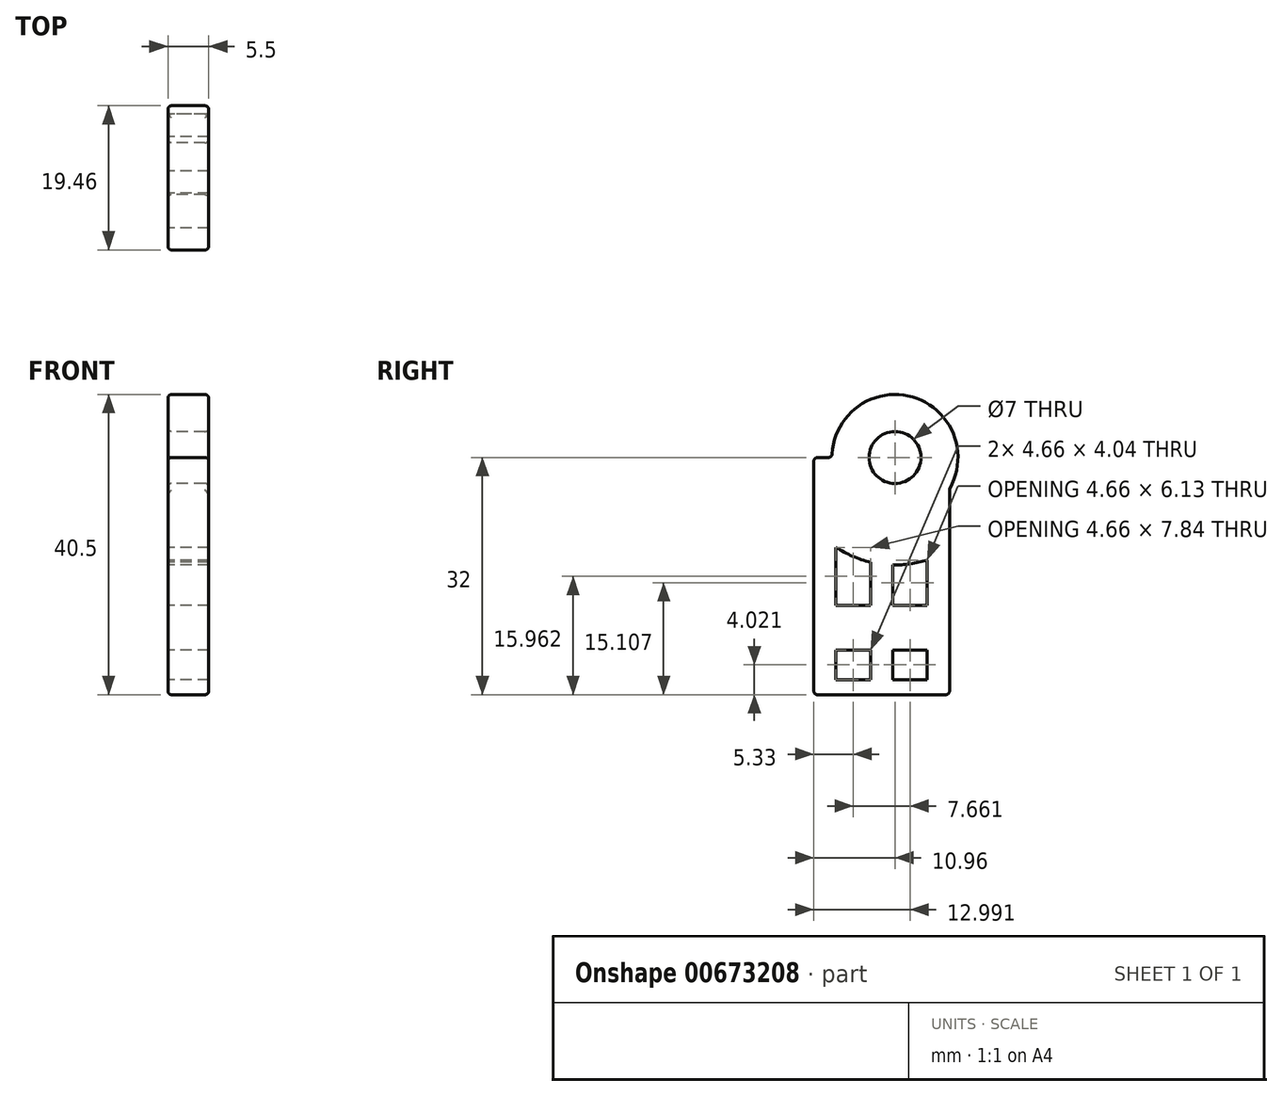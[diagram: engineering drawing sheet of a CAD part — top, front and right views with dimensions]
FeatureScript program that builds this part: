
annotation { "Feature Type Name" : "Feature", "Feature Type Description" : "" }
export const myFeature = defineFeature(function(context is Context, id is Id, definition is map)
    precondition{}
    {
        {
            var Q0;
            Q0=qCreatedBy(makeId("Right.planeOp"),FACE);
            var sketch = newSketch(context, id + "F0", { "sketchPlane" : qUnion([Q0])});
            skCircle(sketch, "E0", {"center": v(0, 0) * mm, "radius": 8.5 * mm});
            skLineSegment(sketch, "E1.bottom", {"start": v(-10.96, 0) * mm, "end": v(-8.5, 0) * mm});
            skLineSegment(sketch, "E1.left", {"start": v(-10.96, 0) * mm, "end": v(-10.96, -30) * mm});
            skLineSegment(sketch, "E2", {"start": v(-0.43, -4.25) * mm, "end": v(7.36, -4.25) * mm, "construction": true});
            skLineSegment(sketch, "E3", {"start": v(7.36, -4.25) * mm, "end": v(7.36, -30) * mm});
            skLineSegment(sketch, "E4", {"start": v(7.36, -30) * mm, "end": v(-10.96, -30) * mm});
            skCircle(sketch, "E5", {"center": v(0, 0) * mm, "radius": 3.5 * mm});
            skSolve(sketch);
        }
        {
            var Q0;
            Q0=makeQuery(id+"F0.imprint","IMPRINT",FACE,{"disambiguationData":[TD([[makeQuery(id+"F0.imprint","IMPRINT",EDGE,{"derivedFrom":sQuery(id+"F0.wireOp",EDGE,"E5")}),-1.0]])]});
            var Q1;
            {var subQ1=sQuery(id+"F0.wireOp",EDGE,"E1.bottom");Q1=makeQuery(id+"F0.imprint","IMPRINT",FACE,{"disambiguationData":[TD([[makeQuery(id+"F0.imprint","IMPRINT",EDGE,{"derivedFrom":subQ1}),-1.0]])]});}
            extrude(context, id + "F1", {"entities" : qUnion([Q0, Q1]), "depth" : 5.5 * mm});
        }
        {
            var Q0;
            {var subQ0=sQuery(id+"F0.wireOp",EDGE,"E4");var subQ1=sQuery(id+"F0.wireOp",EDGE,"E1.left");Q0=makeQuery(id+"FtR0d7urNmnyYv5_1.boolean.opBoolean","MERGE",FACE,{"derivedFrom":[makeQuery(id+"F9VDkFG8JvXqduY_1.boolean.opBoolean","MERGE",FACE,{"derivedFrom":[makeQuery(id+"F1.opExtrude","SWEPT_FACE",FACE,{"disambiguationData":[OSD([subQ0])]}),makeQuery(id+"F9VDkFG8JvXqduY_1.opExtrude","SWEPT_FACE",FACE,{"disambiguationData":[OSD([subQ1,subQ0])]})]}),makeQuery(id+"FtR0d7urNmnyYv5_1.opExtrude","SWEPT_FACE",FACE,{"disambiguationData":[OSD([subQ1,subQ0])]})]});}
            extrude(context, id + "F2", {"entities" : qUnion([Q0]), "operationType" : NewBodyOperationType.ADD, "depth" : 3 * mm});
        }
        {
            var Q0;
            {var subQ0=sQuery(id+"F0.wireOp",EDGE,"E4");Q0=makeQuery(id+"F2.boolean.opBoolean","MERGE",FACE,{"derivedFrom":[makeQuery(id+"F1.opExtrude","CAP_FACE",FACE,{"disambiguationData":[OSD([sQuery(id+"F0.wireOp",EDGE,"E0"),sQuery(id+"F0.wireOp",EDGE,"E1.bottom"),sQuery(id+"F0.wireOp",EDGE,"E1.left"),sQuery(id+"F0.wireOp",EDGE,"E3"),subQ0,sQuery(id+"F0.wireOp",EDGE,"E5")])],"isStart":true}),makeQuery(id+"F2.opExtrude","SWEPT_FACE",FACE,{"disambiguationData":[OSD([subQ0]),TDD([makeQuery(id+"F1.opExtrude","CAP_EDGE",EDGE,{"disambiguationData":[OSD([subQ0])],"isStart":true})])]})]});}
            var sketch = newSketch(context, id + "F3", { "sketchPlane" : qUnion([Q0])});
            skArc(sketch, "E6", {"start": v(-7.36, -8.84) * mm, "mid": v(3.22, -11.04) * mm, "end": v(10.96, -3.48) * mm});
            skLineSegment(sketch, "E7", {"start": v(-7.36, -8.84) * mm, "end": v(-7.36, -33) * mm});
            skLineSegment(sketch, "E8", {"start": v(-7.36, -33) * mm, "end": v(10.96, -33) * mm});
            skLineSegment(sketch, "E9", {"start": v(10.96, -33) * mm, "end": v(10.96, -3.48) * mm});
            skArc(sketch, "E10.0", {"start": v(-4.36, -13.83) * mm, "mid": v(-2.06, -14.35) * mm, "end": v(0.3, -14.5) * mm});
            skLineSegment(sketch, "E10.1", {"start": v(-4.36, -13.83) * mm, "end": v(-4.36, -19.96) * mm});
            skLineSegment(sketch, "E10.2", {"start": v(-4.36, -30) * mm, "end": v(0.3, -30) * mm});
            skLineSegment(sketch, "E10.3", {"start": v(7.96, -30) * mm, "end": v(7.96, -25.96) * mm});
            skLineSegment(sketch, "E11", {"start": v(-4.36, -19.96) * mm, "end": v(0.3, -19.96) * mm});
            skLineSegment(sketch, "E12.trimOffspring", {"start": v(-4.36, -25.96) * mm, "end": v(-4.36, -30) * mm});
            skLineSegment(sketch, "E13.trimOffspring", {"start": v(7.96, -19.96) * mm, "end": v(7.96, -12.12) * mm});
            skLineSegment(sketch, "E14", {"start": v(7.96, -25.96) * mm, "end": v(3.3, -25.96) * mm});
            skPoint(sketch, "E15.start.orphan", {"position": v(-4.36, -21.91) * mm});
            skPoint(sketch, "E16.orphan", {"position": v(7.96, -21.91) * mm});
            skLineSegment(sketch, "E17", {"start": v(1.8, -25.96) * mm, "end": v(1.8, -30) * mm, "construction": true});
            skLineSegment(sketch, "E18", {"start": v(3.3, -30) * mm, "end": v(3.3, -25.96) * mm});
            skLineSegment(sketch, "E19.MirrorCS", {"start": v(0.3, -30) * mm, "end": v(0.3, -25.96) * mm});
            skLineSegment(sketch, "E20.trimOffspring", {"start": v(3.3, -30) * mm, "end": v(7.96, -30) * mm});
            skLineSegment(sketch, "E21.trimOffspring", {"start": v(0.3, -25.96) * mm, "end": v(-4.36, -25.96) * mm});
            skLineSegment(sketch, "E22", {"start": v(1.8, -19.96) * mm, "end": v(1.8, -14.39) * mm, "construction": true});
            skLineSegment(sketch, "E23", {"start": v(3.3, -19.96) * mm, "end": v(3.3, -14.12) * mm});
            skLineSegment(sketch, "E24.MirrorCS", {"start": v(0.3, -19.96) * mm, "end": v(0.3, -14.5) * mm});
            skPoint(sketch, "E25.orphan", {"position": v(0.3, -14.12) * mm});
            skArc(sketch, "E26.trimOffspring", {"start": v(3.3, -14.12) * mm, "mid": v(5.72, -13.33) * mm, "end": v(7.96, -12.12) * mm});
            skLineSegment(sketch, "E27.trimOffspring", {"start": v(3.3, -19.96) * mm, "end": v(7.96, -19.96) * mm});
            skSolve(sketch);
        }
        {
            var Q0;
            Q0=makeQuery(id+"F3.imprint","IMPRINT",FACE,{"disambiguationData":[TD([[makeQuery(id+"F3.imprint","IMPRINT",EDGE,{"derivedFrom":sQuery(id+"F3.wireOp",EDGE,"E10.0")}),-1.0]])]});
            var Q1;
            Q1=makeQuery(id+"F3.imprint","IMPRINT",FACE,{"disambiguationData":[TD([[makeQuery(id+"F3.imprint","IMPRINT",EDGE,{"derivedFrom":sQuery(id+"F3.wireOp",EDGE,"E10.2")}),1.0]])]});
            var Q2;
            Q2=makeQuery(id+"F3.imprint","IMPRINT",FACE,{"disambiguationData":[TD([[makeQuery(id+"F3.imprint","IMPRINT",EDGE,{"derivedFrom":sQuery(id+"F3.wireOp",EDGE,"E13.trimOffspring")}),1.0]])]});
            var Q3;
            Q3=makeQuery(id+"F3.imprint","IMPRINT",FACE,{"disambiguationData":[TD([[makeQuery(id+"F3.imprint","IMPRINT",EDGE,{"derivedFrom":sQuery(id+"F3.wireOp",EDGE,"E10.3")}),1.0]])]});
            extrude(context, id + "F4", {"entities" : qUnion([Q0, Q1, Q2, Q3]), "operationType" : NewBodyOperationType.REMOVE, "oppositeDirection" : true, "depth" : 25 * mm});
        }
        {
            var Q0;
            Q0=makeQuery(id+"F2.opExtrude","CAP_FACE",FACE,{"disambiguationData":[OSD([sQuery(id+"F0.wireOp",EDGE,"E4")])],"isStart":false});
            extrude(context, id + "F5", {"entities" : qUnion([Q0]), "operationType" : NewBodyOperationType.REMOVE, "oppositeDirection" : true, "depth" : 1 * mm});
        }
        {
            var Q0;
            Q0=makeQuery(id+"F1.opExtrude","SWEPT_FACE",FACE,{"disambiguationData":[OSD([sQuery(id+"F0.wireOp",EDGE,"E5")])]});
            var Q1;
            {var subQ0=sQuery(id+"F0.wireOp",EDGE,"E1.left");Q1=makeQuery(id+"F2.boolean.opBoolean","MERGE",FACE,{"derivedFrom":[makeQuery(id+"F1.opExtrude","SWEPT_FACE",FACE,{"disambiguationData":[OSD([subQ0])]}),makeQuery(id+"F2.opExtrude","SWEPT_FACE",FACE,{"disambiguationData":[OSD([subQ0,sQuery(id+"F0.wireOp",EDGE,"E4")])]})]});}
            var Q2;
            Q2=makeQuery(id+"F1.opExtrude","SWEPT_FACE",FACE,{"disambiguationData":[OSD([sQuery(id+"F0.wireOp",EDGE,"E1.bottom")])]});
            var Q3;
            Q3=makeQuery(id+"F1.opExtrude","SWEPT_FACE",FACE,{"disambiguationData":[OSD([sQuery(id+"F0.wireOp",EDGE,"E0")])]});
            var Q4;
            Q4=makeQuery(id+"F5.boolean.opBoolean","COPY",FACE,{"derivedFrom":makeQuery(id+"F5.opExtrude","CAP_FACE",FACE,{"disambiguationData":[OSD([sQuery(id+"F0.wireOp",EDGE,"E4")])],"isStart":false})});
            fillet(context, id + "F6", {"entities" : qUnion([Q0, Q1, Q2, Q3, Q4]), "radius" : .5 * mm, "tangentPropagation" : true, "allowEdgeOverflow" : false});
        }
    });
